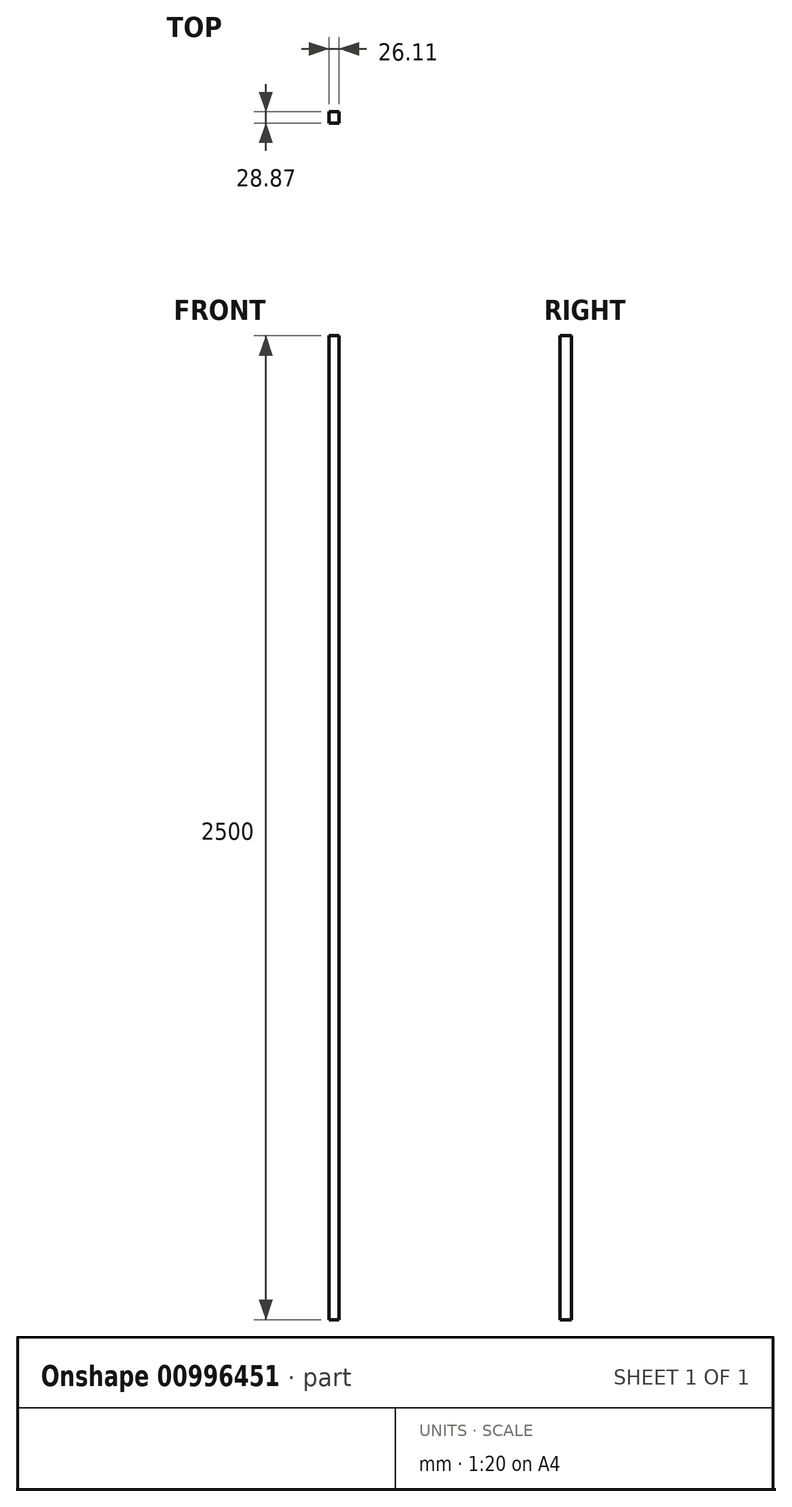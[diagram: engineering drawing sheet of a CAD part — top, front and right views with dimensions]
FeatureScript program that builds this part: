
annotation { "Feature Type Name" : "Feature", "Feature Type Description" : "" }
export const myFeature = defineFeature(function(context is Context, id is Id, definition is map)
    precondition{}
    {
        {
            var Q0;
            Q0=qCreatedBy(makeId("Top.planeOp"),FACE);
            var sketch = newSketch(context, id + "F0", { "sketchPlane" : qUnion([Q0])});
            skLineSegment(sketch, "E0.bottom", {"start": v(40.87, 44.19) * mm, "end": v(-56.43, 44.19) * mm});
            skLineSegment(sketch, "E0.top", {"start": v(40.87, -42.94) * mm, "end": v(-56.43, -42.94) * mm});
            skLineSegment(sketch, "E0.left", {"start": v(40.87, 44.19) * mm, "end": v(40.87, -42.94) * mm});
            skLineSegment(sketch, "E0.right", {"start": v(-56.43, 44.19) * mm, "end": v(-56.43, -42.94) * mm});
            skLineSegment(sketch, "E1.bottom", {"start": v(66.98, 86.96) * mm, "end": v(40.87, 86.96) * mm});
            skLineSegment(sketch, "E1.top", {"start": v(66.98, 58.1) * mm, "end": v(40.87, 58.1) * mm});
            skLineSegment(sketch, "E1.left", {"start": v(66.98, 86.96) * mm, "end": v(66.98, 58.1) * mm});
            skLineSegment(sketch, "E1.right", {"start": v(40.87, 86.96) * mm, "end": v(40.87, 58.1) * mm});
            skSolve(sketch);
        }
        {
            var Q0;
            Q0=makeQuery(id+"F0.imprint","IMPRINT",FACE,{"disambiguationData":[TD([[makeQuery(id+"F0.imprint","IMPRINT",EDGE,{"derivedFrom":sQuery(id+"F0.wireOp",EDGE,"E1.bottom")}),1.0]])]});
            extrude(context, id + "F1", {"entities" : qUnion([Q0]), "depth" : 2500 * mm, "offsetDistance" : 25.4 * mm});
        }
    });
